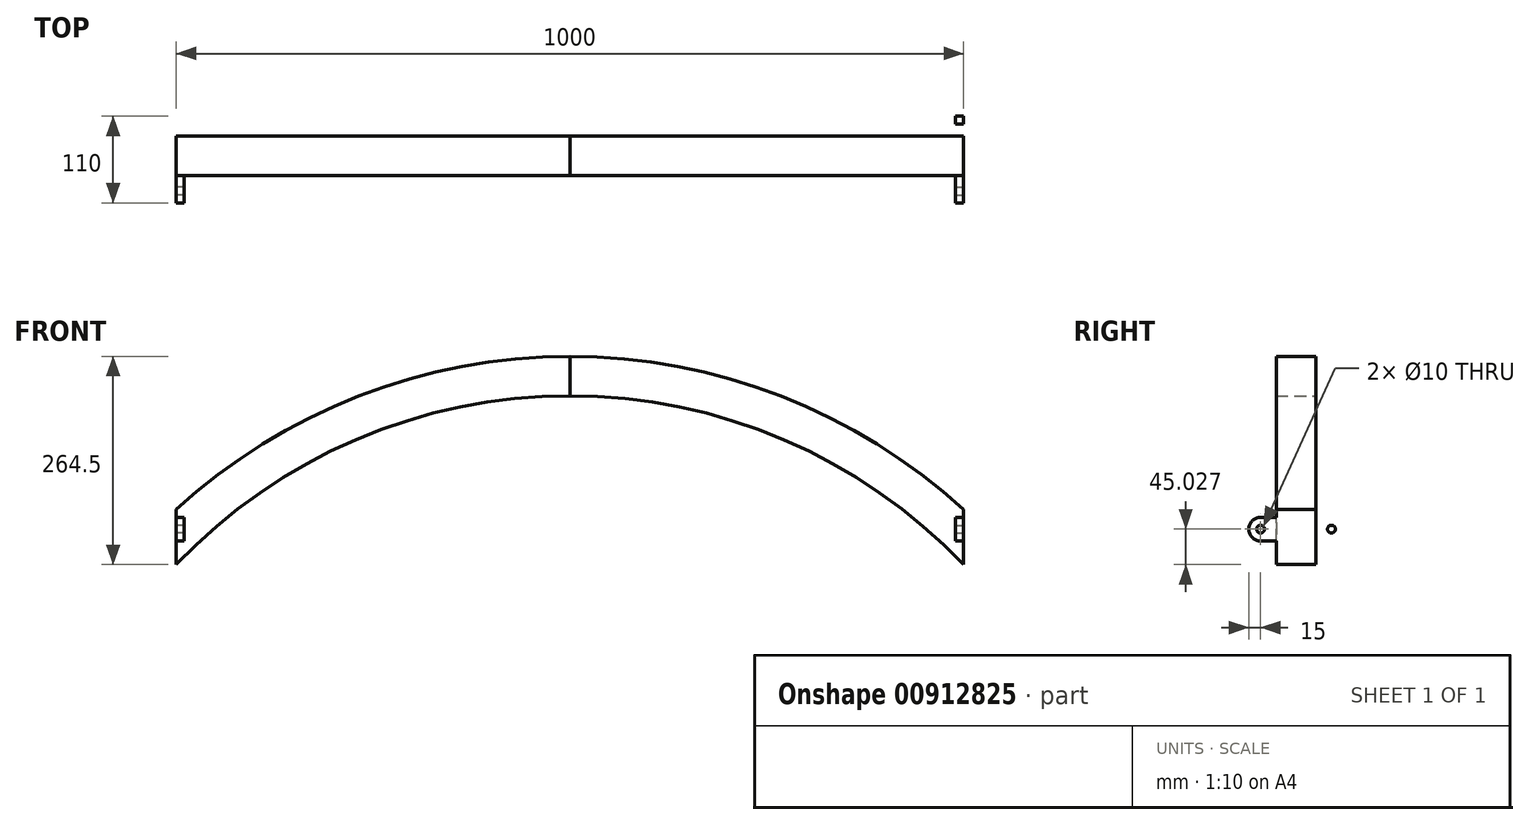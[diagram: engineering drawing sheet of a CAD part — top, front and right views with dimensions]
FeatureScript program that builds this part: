
annotation { "Feature Type Name" : "Feature", "Feature Type Description" : "" }
export const myFeature = defineFeature(function(context is Context, id is Id, definition is map)
    precondition{}
    {
        {
            var Q0;
            Q0=qCreatedBy(makeId("Front.planeOp"),FACE);
            var sketch = newSketch(context, id + "F0", { "sketchPlane" : qUnion([Q0])});
            skLineSegment(sketch, "E0", {"start": v(0, 0) * mm, "end": v(0, 690) * mm, "construction": true});
            skArc(sketch, "E1", {"start": v(0, 690) * mm, "mid": v(272.03, 634.11) * mm, "end": v(500, 475.5) * mm});
            skLineSegment(sketch, "E2", {"start": v(500, 475.5) * mm, "end": v(0, 475.5) * mm, "construction": true});
            skSolve(sketch);
        }
        {
            var Q0;
            Q0=qCreatedBy(makeId("Right.planeOp"),FACE);
            var sketch = newSketch(context, id + "F1", { "sketchPlane" : qUnion([Q0])});
            skLineSegment(sketch, "E3", {"start": v(0, 690) * mm, "end": v(0, 740) * mm});
            skLineSegment(sketch, "E4", {"start": v(0, 740) * mm, "end": v(-50, 740) * mm});
            skLineSegment(sketch, "E5", {"start": v(-50, 740) * mm, "end": v(-50, 690) * mm});
            skLineSegment(sketch, "E6", {"start": v(-50, 690) * mm, "end": v(0, 690) * mm});
            skSolve(sketch);
        }
        {
            var Q0;
            Q0=makeQuery(id+"F1.imprint","IMPRINT",FACE,{"disambiguationData":[TD([[makeQuery(id+"F1.imprint","IMPRINT",EDGE,{"derivedFrom":sQuery(id+"F1.wireOp",EDGE,"E3")}),1.0]])]});
            var Q1;
            Q1=sQuery(id+"F0.wireOp",EDGE,"E1");
            sweep(context, id + "F2", {"profiles" : qUnion([Q0]), "path" : qUnion([Q1])});
        }
        {
            var Q0;
            Q0=qCreatedBy(makeId("Front.planeOp"),FACE);
            var sketch = newSketch(context, id + "F3", { "sketchPlane" : qUnion([Q0])});
            skLineSegment(sketch, "E7", {"start": v(0, 0) * mm, "end": v(500, 0) * mm, "construction": true});
            skLineSegment(sketch, "E8", {"start": v(500, 0) * mm, "end": v(500, 583.3) * mm, "construction": true});
            skLineSegment(sketch, "E9", {"start": v(500, 583.3) * mm, "end": v(500, 449.77) * mm});
            skLineSegment(sketch, "E10", {"start": v(500, 449.77) * mm, "end": v(564.37, 449.77) * mm});
            skLineSegment(sketch, "E11", {"start": v(564.37, 449.77) * mm, "end": v(564.37, 583.3) * mm});
            skLineSegment(sketch, "E12", {"start": v(564.37, 583.3) * mm, "end": v(500, 583.3) * mm});
            skSolve(sketch);
        }
        {
            var Q0;
            Q0 = qSketchRegion(id + "F3", true);
            extrude(context, id + "F4", {"entities" : qUnion([Q0]), "operationType" : NewBodyOperationType.REMOVE, "depth" : 91 * mm, "offsetDistance" : 25 * mm});
        }
        {
            var Q0;
            Q0=makeQuery(id+"F4.boolean.opBoolean","COPY",FACE,{"derivedFrom":makeQuery(id+"F4.opExtrude","SWEPT_FACE",FACE,{"disambiguationData":[OSD([sQuery(id+"F3.wireOp",EDGE,"E9")])]})});
            var sketch = newSketch(context, id + "F5", { "sketchPlane" : qUnion([Q0])});
            skLineSegment(sketch, "E13", {"start": v(-50, 545.53) * mm, "end": v(-50, 535.53) * mm, "construction": true});
            skLineSegment(sketch, "E14", {"start": v(-85, 535.53) * mm, "end": v(-50, 535.53) * mm, "construction": true});
            skLineSegment(sketch, "E15", {"start": v(-50, 535.53) * mm, "end": v(-50, 505.53) * mm, "construction": true});
            skLineSegment(sketch, "E16", {"start": v(-120.01, 505.53) * mm, "end": v(59.97, 505.53) * mm, "construction": true});
            skLineSegment(sketch, "E17", {"start": v(-50, 535.53) * mm, "end": v(-70, 535.53) * mm});
            skLineSegment(sketch, "E18", {"start": v(-85, 520.53) * mm, "end": v(-85, 520.53) * mm});
            skLineSegment(sketch, "E19", {"start": v(-70, 505.53) * mm, "end": v(-50, 505.53) * mm});
            skPoint(sketch, "E20.orphan", {"position": v(-119.56, 535.53) * mm});
            skPoint(sketch, "E21.visualSharp", {"position": v(-85, 535.53) * mm});
            skArc(sketch, "E21.filletArc", {"start": v(-70, 535.53) * mm, "mid": v(-80.6, 531.13) * mm, "end": v(-85, 520.53) * mm});
            skPoint(sketch, "E22.visualSharp", {"position": v(-85, 505.53) * mm});
            skArc(sketch, "E22.filletArc", {"start": v(-85, 520.53) * mm, "mid": v(-80.6, 509.92) * mm, "end": v(-70, 505.53) * mm});
            skLineSegment(sketch, "E23", {"start": v(-70, 520.53) * mm, "end": v(-50, 520.53) * mm, "construction": true});
            skCircle(sketch, "E24", {"center": v(-70, 520.53) * mm, "radius": 5 * mm});
            skLineSegment(sketch, "E25", {"start": v(-25, 545.53) * mm, "end": v(-25, 475.5) * mm, "construction": true});
            skCircle(sketch, "E26.MirrorC", {"center": v(20, 520.53) * mm, "radius": 5 * mm});
            skLineSegment(sketch, "E27.MirrorCS", {"start": v(35, 535.53) * mm, "end": v(0, 535.53) * mm, "construction": true});
            skArc(sketch, "E28.MirrorCS", {"start": v(20, 535.53) * mm, "mid": v(30.6, 531.13) * mm, "end": v(35, 520.53) * mm});
            skArc(sketch, "E29.MirrorCS", {"start": v(35, 520.53) * mm, "mid": v(30.6, 509.92) * mm, "end": v(20, 505.53) * mm});
            skLineSegment(sketch, "E30.MirrorCS", {"start": v(70.01, 505.53) * mm, "end": v(-109.97, 505.53) * mm, "construction": true});
            skLineSegment(sketch, "E31", {"start": v(20, 505.53) * mm, "end": v(0, 505.53) * mm});
            skLineSegment(sketch, "E32", {"start": v(20, 535.53) * mm, "end": v(0, 535.53) * mm});
            skSolve(sketch);
        }
        {
            var Q0;
            {var subQ1=sQuery(id+"F5.wireOp",EDGE,"E17");Q0=makeQuery(id+"F5.imprint","IMPRINT",FACE,{"disambiguationData":[TD([[makeQuery(id+"F5.imprint","IMPRINT",EDGE,{"derivedFrom":subQ1}),1.0]])]});}
            var Q1;
            Q1=makeQuery(id+"F5.imprint","IMPRINT",FACE,{"disambiguationData":[TD([[makeQuery(id+"F5.imprint","IMPRINT",EDGE,{"derivedFrom":sQuery(id+"F5.wireOp",EDGE,"E26.MirrorC")}),1.0]])]});
            extrude(context, id + "F6", {"entities" : qUnion([Q0, Q1]), "operationType" : NewBodyOperationType.ADD, "oppositeDirection" : true, "depth" : 10 * mm, "offsetDistance" : 25 * mm});
        }
        {
            var Q0;
            Q0=makeQuery(id+"F2.opSweep","SWEPT_BODY",BODY,{"disambiguationData":[OSD([sQuery(id+"F0.wireOp",EDGE,"E1"),sQuery(id+"F1.wireOp",EDGE,"E3"),sQuery(id+"F1.wireOp",EDGE,"E4"),sQuery(id+"F1.wireOp",EDGE,"E5"),sQuery(id+"F1.wireOp",EDGE,"E6")])]});
            var Q1;
            Q1=makeQuery(id+"F2.opSweep","CAP_FACE",FACE,{"disambiguationData":[OSD([sQuery(id+"F0.wireOp",VERTEX,"E1.start"),sQuery(id+"F1.wireOp",EDGE,"E3"),sQuery(id+"F1.wireOp",EDGE,"E4"),sQuery(id+"F1.wireOp",EDGE,"E5"),sQuery(id+"F1.wireOp",EDGE,"E6")])],"isStart":true});
            mirror(context, id + "F7", {"operationType" : NewBodyOperationType.ADD, "entities" : qUnion([Q0]), "mirrorPlane" : qUnion([Q1])});
        }
    });
